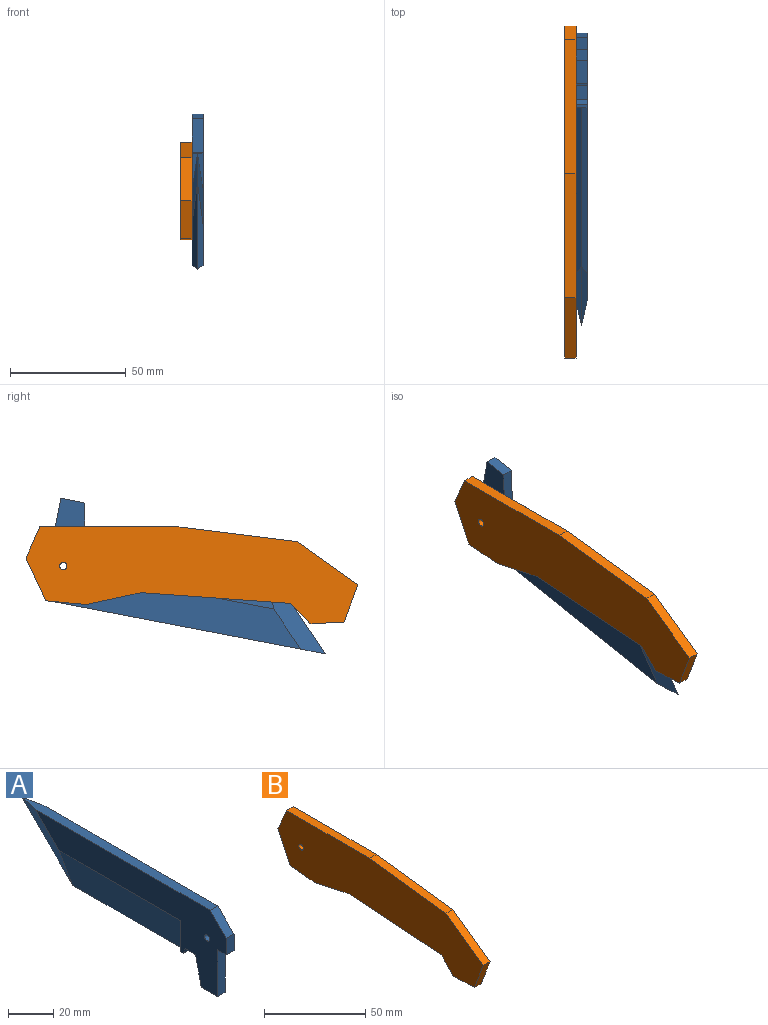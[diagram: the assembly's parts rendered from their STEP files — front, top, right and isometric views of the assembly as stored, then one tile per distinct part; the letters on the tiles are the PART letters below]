
ASSEMBLY  parts=2 mates=1
PART A: 19 faces, bbox 4.8x130.2x44.5 mm
  f0: plane 120.02x4.76mm, normal (0,0,1), area 546mm2, adj f1,f2,f5,f6,f18
  f1: plane 119.43x44.45mm, normal (-1,0,0), area 2137.4mm2, adj f0,f3,f6,f8,f9,f10,f11,f12
  f2: plane 119.43x44.45mm, normal (1,0,0), area 2137.4mm2, adj f0,f4,f5,f7,f8,f9,f10,f11
  f3: plane 76.05x16.94mm, normal (-0.99,0,-0.14), area 1248.2mm2, adj f1,f4,f6,f17
  f4: plane 76.05x16.94mm, normal (0.99,0,-0.14), area 1248.2mm2, adj f2,f3,f5,f7
  f5: plane 31.75x31.75mm, normal (0.95,0.21,-0.21), area 262mm2, adj f0,f2,f4,f6
  f6: plane 31.75x31.75mm, normal (-0.95,0.21,-0.21), area 262mm2, adj f0,f1,f3,f5
  f7: plane 16.94x2.38mm, normal (0,1,0), area 20.2mm2, adj f2,f4,f15
  f8: plane 8.89x4.76mm, normal (0,-1,0), area 42.3mm2, adj f1,f2,f9,f18
  f9: plane 5.53x4.76mm, normal (0,0,-1), area 26.3mm2, adj f1,f2,f8,f10
  f10: plane 25.4x4.76mm, normal (0,-1,0), area 121mm2, adj f1,f2,f9,f11
  f11: plane 10.16x4.76mm, normal (0,0,-1), area 48.4mm2, adj f1,f2,f10,f12
  f12: plane 15.88x4.76mm, normal (0,0.97,-0.22), area 77.6mm2, adj f1,f2,f11,f13
  f13: plane 6.35x4.76mm, normal (0,0,-1), area 30.2mm2, adj f1,f2,f12,f14
  f14: plane 4.76x3.18mm, normal (0,-0.93,-0.38), area 16.3mm2, adj f1,f2,f13,f15
  f15: plane 4.76x1.59mm, normal (0,0,-1), area 7.6mm2, adj f1,f2,f7,f14,f17
  f16: cylinder r=1.59mm len=4.76mm, axis (-1,0,0), area 47.5mm2, adj f1,f2
  f17: plane 16.94x2.38mm, normal (0,1,0), area 20.2mm2, adj f1,f3,f15
  f18: plane 10.16x10.16mm, normal (0,-0.71,0.71), area 68.4mm2, adj f0,f1,f2,f8
PART B: 14 faces, bbox 4.8x143.2x42 mm
  f0: plane 17.43x4.76mm, normal (0,0.09,-1), area 83.4mm2, adj f1,f10,f12,f13
  f1: plane 18.37x8.52mm, normal (0,0.91,-0.42), area 96.4mm2, adj f0,f2,f12,f13
  f2: plane 13.75x5.99mm, normal (0,0.92,0.4), area 71.4mm2, adj f1,f3,f12,f13
  f3: plane 57.83x4.76mm, normal (0,0,1), area 275.4mm2, adj f2,f4,f12,f13
  f4: plane 53.32x6.63mm, normal (0,-0.12,0.99), area 255.9mm2, adj f3,f5,f12,f13
  f5: plane 26.05x18.53mm, normal (0,-0.58,0.81), area 152.2mm2, adj f4,f6,f12,f13
  f6: plane 16.24x6.08mm, normal (0,-0.94,-0.35), area 82.6mm2, adj f5,f7,f12,f13
  f7: plane 14.63x4.76mm, normal (0,-0.04,-1), area 69.7mm2, adj f6,f8,f12,f13
  f8: plane 8.74x8.37mm, normal (0,0.72,-0.69), area 57.6mm2, adj f7,f9,f12,f13
  f9: plane 64.46x4.76mm, normal (0,0.07,-1), area 307.8mm2, adj f8,f10,f12,f13
  f10: plane 23.7x5.09mm, normal (0,-0.21,-0.98), area 115.4mm2, adj f0,f9,f12,f13
  f11: cylinder r=1.59mm len=4.76mm, axis (1,0,0), area 47.5mm2, adj f12,f13
  f12: plane 143.18x41.98mm, normal (-1,0,0), area 3988.1mm2, adj f0,f1,f2,f3,f4,f5,f6,f7
  f13: plane 143.18x41.98mm, normal (1,0,0), area 3988.1mm2, adj f0,f1,f2,f3,f4,f5,f6,f7
PLACE A rot(axis=(-1,0,0),169.2deg) t=(-0.15,-117.45,-27.86)mm
PLACE B rot(axis=(1,0,0),0deg) t=(-0.15,15.96,-15.19)mm
MATE revolute B.f11 <-> A.f16  axis (1,0,0) through (-2.53,-51.34,-15.19)mm
